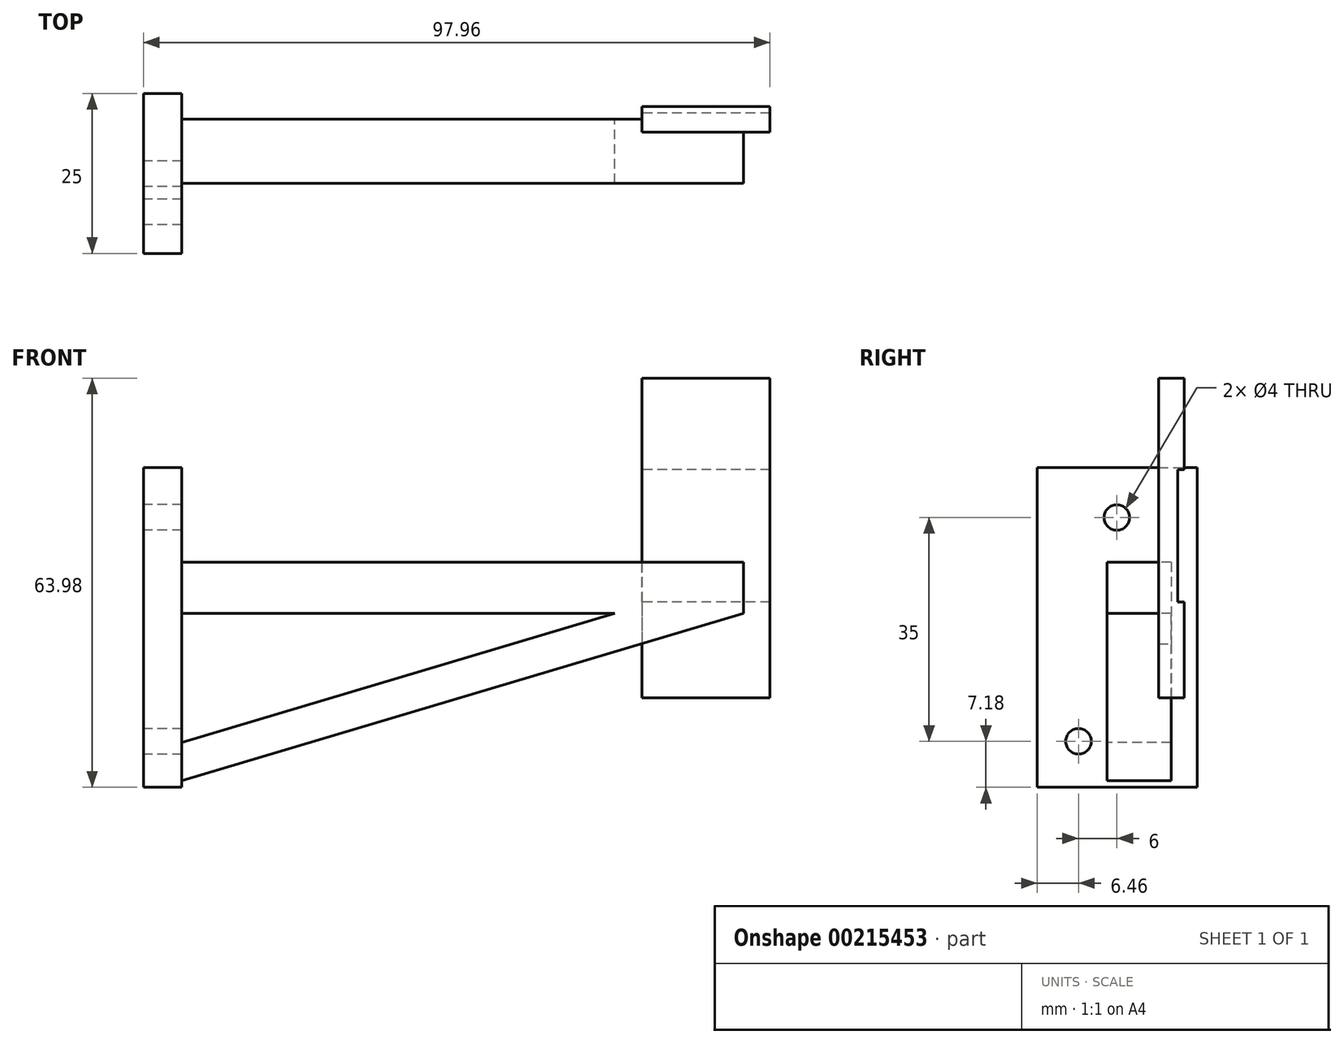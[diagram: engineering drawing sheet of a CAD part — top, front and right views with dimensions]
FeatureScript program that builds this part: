
annotation { "Feature Type Name" : "Feature", "Feature Type Description" : "" }
export const myFeature = defineFeature(function(context is Context, id is Id, definition is map)
    precondition{}
    {
        {
            var Q0;
            Q0=qCreatedBy(makeId("Right.planeOp"),FACE);
            var sketch = newSketch(context, id + "F0", { "sketchPlane" : qUnion([Q0])});
            skCircle(sketch, "E0", {"center": v(0, 0) * mm, "radius": 2 * mm});
            skCircle(sketch, "E1", {"center": v(6, 35) * mm, "radius": 2 * mm});
            skLineSegment(sketch, "E2.bottom", {"start": v(-6.46, -7.18) * mm, "end": v(18.54, -7.18) * mm});
            skLineSegment(sketch, "E2.top", {"start": v(-6.46, 42.82) * mm, "end": v(18.54, 42.82) * mm});
            skLineSegment(sketch, "E2.left", {"start": v(-6.46, -7.18) * mm, "end": v(-6.46, 42.82) * mm});
            skLineSegment(sketch, "E2.right", {"start": v(18.54, -7.18) * mm, "end": v(18.54, 42.82) * mm});
            skSolve(sketch);
        }
        {
            var Q0;
            Q0=makeQuery(id+"F0.imprint","IMPRINT",FACE,{"disambiguationData":[TD([[makeQuery(id+"F0.imprint","IMPRINT",EDGE,{"derivedFrom":sQuery(id+"F0.wireOp",EDGE,"E0")}),-1.0]])]});
            var Q1;
            Q1=sQuery(id+"F0.wireOp",EDGE,"E2.bottom");
            var Q2;
            Q2=sQuery(id+"F0.wireOp",EDGE,"E0");
            var Q3;
            Q3=sQuery(id+"F0.wireOp",EDGE,"E1");
            var Q4;
            Q4=sQuery(id+"F0.wireOp",EDGE,"E2.top");
            var Q5;
            Q5=sQuery(id+"F0.wireOp",EDGE,"E2.left");
            var Q6;
            Q6=sQuery(id+"F0.wireOp",EDGE,"E2.right");
            extrude(context, id + "F1", {"entities" : qUnion([Q0]), "surfaceEntities" : qUnion([Q1, Q2, Q3, Q4, Q5, Q6]), "depth" : 6 * mm});
        }
        {
            var Q0;
            Q0=qCreatedBy(makeId("Front.planeOp"),FACE);
            cPlane(context, id + "F2", {"entities" : qUnion([Q0]), "cplaneType" : CPlaneType.OFFSET, "offset" : 14.5 * mm, "oppositeDirection" : true, "width" : 150 * mm, "height" : 150 * mm});
        }
        {
            var Q0;
            Q0=qCreatedBy(id+"F2.planeOp",FACE);
            var sketch = newSketch(context, id + "F3", { "sketchPlane" : qUnion([Q0])});
            skLineSegment(sketch, "E3.bottom", {"start": v(3.82, 28) * mm, "end": v(93.82, 28) * mm});
            skLineSegment(sketch, "E3.top", {"start": v(3.82, 20) * mm, "end": v(93.82, 20) * mm});
            skLineSegment(sketch, "E3.left", {"start": v(3.82, 28) * mm, "end": v(3.82, 20) * mm});
            skLineSegment(sketch, "E3.right", {"start": v(93.82, 28) * mm, "end": v(93.82, 20) * mm});
            skLineSegment(sketch, "E4", {"start": v(93.82, 20) * mm, "end": v(4.43, -6.64) * mm});
            skLineSegment(sketch, "E5", {"start": v(4.43, -6.64) * mm, "end": v(4.43, -0.64) * mm});
            skLineSegment(sketch, "E6", {"start": v(4.43, -0.64) * mm, "end": v(73.67, 20) * mm});
            skSolve(sketch);
        }
        {
            var Q0;
            Q0 = qSketchRegion(id + "F3", true);
            extrude(context, id + "F4", {"entities" : qUnion([Q0]), "operationType" : NewBodyOperationType.ADD, "depth" : 10 * mm});
        }
        {
            var Q0;
            Q0=qCreatedBy(makeId("Front.planeOp"),FACE);
            cPlane(context, id + "F5", {"entities" : qUnion([Q0]), "cplaneType" : CPlaneType.OFFSET, "offset" : 12.5 * mm, "oppositeDirection" : true, "width" : 150 * mm, "height" : 150 * mm});
        }
        {
            var Q0;
            Q0=qCreatedBy(id+"F5.planeOp",FACE);
            var sketch = newSketch(context, id + "F6", { "sketchPlane" : qUnion([Q0])});
            skLineSegment(sketch, "E7.bottom", {"start": v(77.96, 56.8) * mm, "end": v(97.96, 56.8) * mm});
            skLineSegment(sketch, "E7.top", {"start": v(77.96, 6.8) * mm, "end": v(97.96, 6.8) * mm});
            skLineSegment(sketch, "E7.left", {"start": v(77.96, 56.8) * mm, "end": v(77.96, 6.8) * mm});
            skLineSegment(sketch, "E7.right", {"start": v(97.96, 56.8) * mm, "end": v(97.96, 6.8) * mm});
            skSolve(sketch);
        }
        {
            var Q0;
            Q0 = qSketchRegion(id + "F6", true);
            extrude(context, id + "F7", {"entities" : qUnion([Q0]), "operationType" : NewBodyOperationType.ADD, "oppositeDirection" : true, "depth" : 4 * mm});
        }
        {
            var Q0;
            Q0=qCreatedBy(makeId("Front.planeOp"),FACE);
            cPlane(context, id + "F8", {"entities" : qUnion([Q0]), "cplaneType" : CPlaneType.OFFSET, "offset" : 16.5 * mm, "oppositeDirection" : true, "width" : 150 * mm, "height" : 150 * mm});
        }
        {
            var Q0;
            Q0=qCreatedBy(id+"F8.planeOp",FACE);
            var sketch = newSketch(context, id + "F9", { "sketchPlane" : qUnion([Q0])});
            skLineSegment(sketch, "E8.bottom", {"start": v(102.88, 42.47) * mm, "end": v(72.88, 42.47) * mm});
            skLineSegment(sketch, "E8.top", {"start": v(102.88, 21.77) * mm, "end": v(72.88, 21.77) * mm});
            skLineSegment(sketch, "E8.left", {"start": v(102.88, 42.47) * mm, "end": v(102.88, 21.77) * mm});
            skLineSegment(sketch, "E8.right", {"start": v(72.88, 42.47) * mm, "end": v(72.88, 21.77) * mm});
            skSolve(sketch);
        }
        {
            var Q0;
            Q0 = qSketchRegion(id + "F9", true);
            extrude(context, id + "F10", {"entities" : qUnion([Q0]), "operationType" : NewBodyOperationType.REMOVE, "depth" : 1 * mm});
        }
    });
